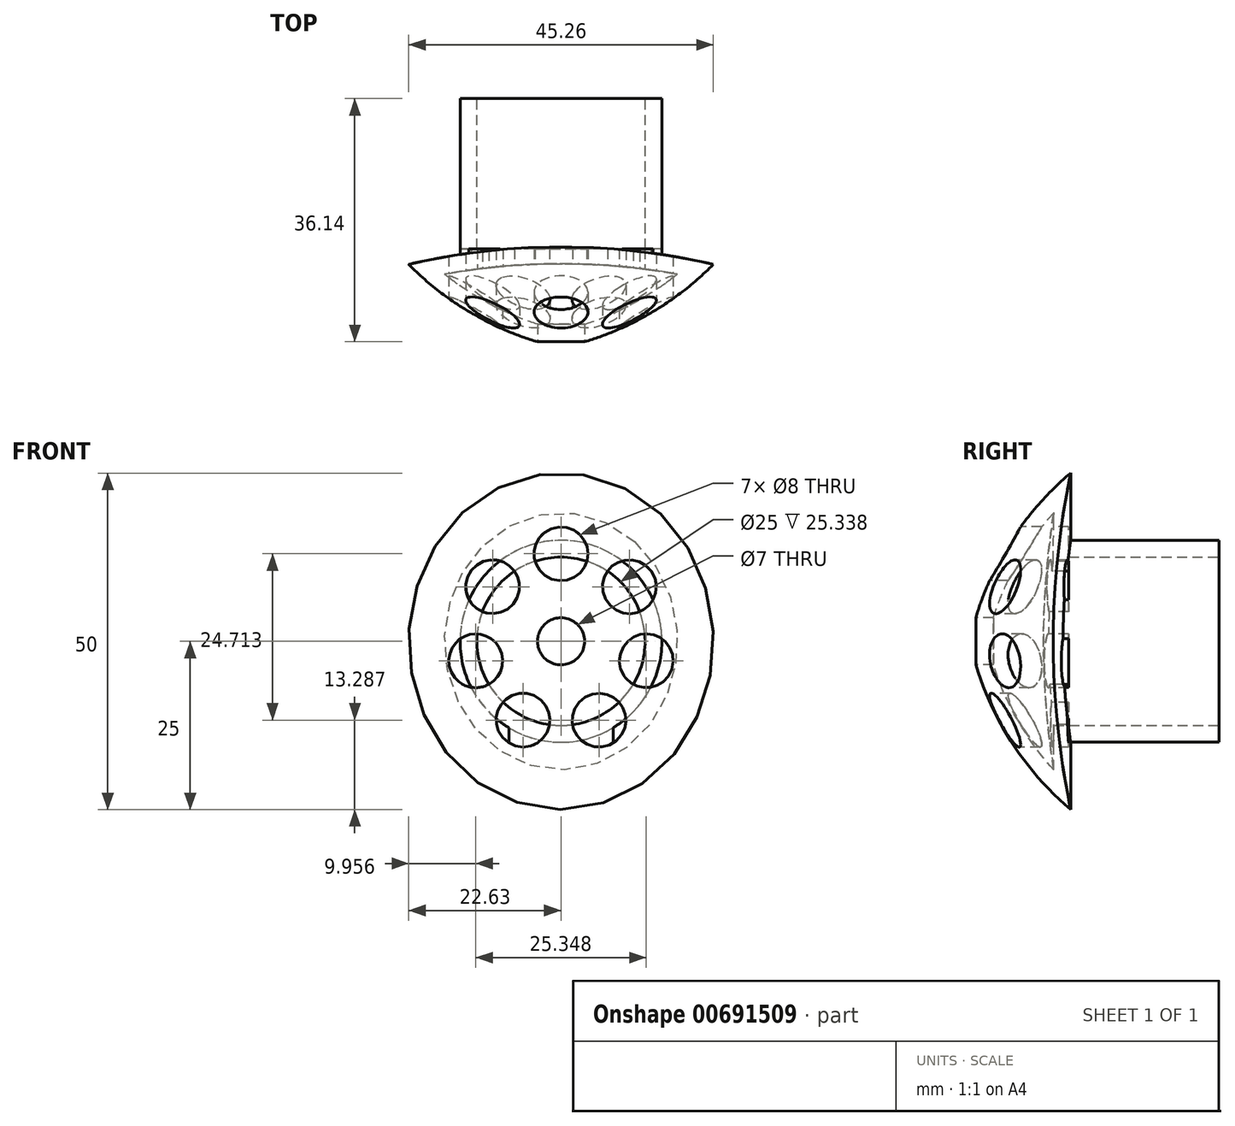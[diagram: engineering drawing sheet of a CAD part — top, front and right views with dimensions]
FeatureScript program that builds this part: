
annotation { "Feature Type Name" : "Feature", "Feature Type Description" : "" }
export const myFeature = defineFeature(function(context is Context, id is Id, definition is map)
    precondition{}
    {
        {
            var Q0;
            Q0=qCreatedBy(makeId("Right.planeOp"),FACE);
            var sketch = newSketch(context, id + "F0", { "sketchPlane" : qUnion([Q0])});
            skLineSegment(sketch, "E0", {"start": v(0, 0) * mm, "end": v(-102.49, 0) * mm, "construction": true});
            skSolve(sketch);
        }
        {
            var Q0;
            Q0=qCreatedBy(makeId("Right.planeOp"),FACE);
            var sketch = newSketch(context, id + "F1", { "sketchPlane" : qUnion([Q0])});
            skLineSegment(sketch, "E1", {"start": v(2.96, 0) * mm, "end": v(2.96, -25) * mm});
            skArc(sketch, "E2", {"start": v(-12.04, 0) * mm, "mid": v(-6.62, -13.75) * mm, "end": v(2.96, -25) * mm});
            skLineSegment(sketch, "E3", {"start": v(2.96, 0) * mm, "end": v(-12.04, 0) * mm});
            skSolve(sketch);
        }
        {
            var Q0;
            Q0 = qSketchRegion(id + "F1", true);
            var Q1;
            Q1=sQuery(id+"F0.wireOp",EDGE,"E0");
            revolve(context, id + "F2", {"entities" : qUnion([Q0]), "axis" : qUnion([Q1]), "revolveType" : RevolveType.FULL});
        }
        {
            var Q0;
            Q0=qCreatedBy(makeId("Top.planeOp"),FACE);
            var sketch = newSketch(context, id + "F3", { "sketchPlane" : qUnion([Q0])});
            skLineSegment(sketch, "E4", {"start": v(0, 2.96) * mm, "end": v(0, -97.04) * mm, "construction": true});
            skCircle(sketch, "E5", {"center": v(0, -97.04) * mm, "radius": 100 * mm});
            skLineSegment(sketch, "E6.0", {"start": v(-25, 2.96) * mm, "end": v(25, 2.96) * mm, "construction": true});
            skCircle(sketch, "E7", {"center": v(0, -97.04) * mm, "radius": 103.08 * mm});
            skSolve(sketch);
        }
        {
            var Q0;
            Q0 = qSketchRegion(id + "F3", true);
            extrude(context, id + "F4", {"entities" : qUnion([Q0]), "operationType" : NewBodyOperationType.REMOVE, "endBound" : BoundingType.THROUGH_ALL, "oppositeDirection" : true, "depth" : 25 * mm, "offsetDistance" : 25 * mm, "hasSecondDirection" : true, "secondDirectionBound" : SecondDirectionBoundingType.THROUGH_ALL, "secondDirectionOppositeDirection" : false, "secondDirectionDepth" : 25 * mm});
        }
        {
            var Q0;
            Q0=qCreatedBy(makeId("Front.planeOp"),FACE);
            var sketch = newSketch(context, id + "F5", { "sketchPlane" : qUnion([Q0])});
            skCircle(sketch, "E8", {"center": v(0, 0) * mm, "radius": 15 * mm});
            skSolve(sketch);
        }
        {
            var Q0;
            Q0 = qSketchRegion(id + "F5", true);
            extrude(context, id + "F6", {"entities" : qUnion([Q0]), "operationType" : NewBodyOperationType.ADD, "endBound" : BoundingType.UP_TO_NEXT, "depth" : 25 * mm, "offsetDistance" : 25 * mm, "hasSecondDirection" : true, "secondDirectionOppositeDirection" : true, "secondDirectionDepth" : 25 * mm});
        }
        {
            var Q0;
            Q0=makeQuery(id+"F6.opExtrude","CAP_FACE",FACE,{"disambiguationData":[OSD([sQuery(id+"F5.wireOp",EDGE,"E8")])],"isStart":true});
            shell(context, id + "F7", {"entities" : qUnion([Q0]), "thickness" : 2.5 * mm});
        }
        {
            var Q0;
            Q0=makeQuery(id+"F2.opRevolve","SWEPT_VERTEX",VERTEX,{"disambiguationData":[OSD([sQuery(id+"F1.wireOp",EDGE,"E2"),sQuery(id+"F1.wireOp",EDGE,"E3")])]});
            var Q1;
            Q1=makeQuery(id+"F6.opExtrude","SWEPT_FACE",FACE,{"disambiguationData":[OSD([sQuery(id+"F5.wireOp",EDGE,"E8")])]});
            cPlane(context, id + "F8", {"entities" : qUnion([Q0, Q1]), "cplaneType" : CPlaneType.LINE_POINT, "offset" : 25 * mm, "width" : 150 * mm, "height" : 150 * mm});
        }
        {
            var Q0;
            Q0=qCreatedBy(id+"F8.planeOp",FACE);
            var sketch = newSketch(context, id + "F9", { "sketchPlane" : qUnion([Q0])});
            skCircle(sketch, "E9", {"center": v(0, 0) * mm, "radius": 13 * mm, "construction": true});
            skLineSegment(sketch, "E10", {"start": v(0, 32.06) * mm, "end": v(0, -35.42) * mm, "construction": true});
            skCircle(sketch, "E11", {"center": v(0, 13) * mm, "radius": 4 * mm});
            skCircle(sketch, "E12.1.0", {"center": v(-10.16, 8.1) * mm, "radius": 4 * mm});
            skCircle(sketch, "E12.2.0", {"center": v(-12.67, -2.9) * mm, "radius": 4 * mm});
            skCircle(sketch, "E12.3.0", {"center": v(-5.64, -11.71) * mm, "radius": 4 * mm});
            skCircle(sketch, "E12.4.0", {"center": v(5.64, -11.71) * mm, "radius": 4 * mm});
            skCircle(sketch, "E12.5.0", {"center": v(12.67, -2.9) * mm, "radius": 4 * mm});
            skCircle(sketch, "E12.6.0", {"center": v(10.16, 8.1) * mm, "radius": 4 * mm});
            skCircle(sketch, "E13", {"center": v(0, 0) * mm, "radius": 3.5 * mm});
            skSolve(sketch);
        }
        {
            var Q0;
            Q0 = qSketchRegion(id + "F9", true);
            extrude(context, id + "F10", {"entities" : qUnion([Q0]), "operationType" : NewBodyOperationType.REMOVE, "depth" : 14.7 * mm, "offsetDistance" : 25 * mm});
        }
    });
